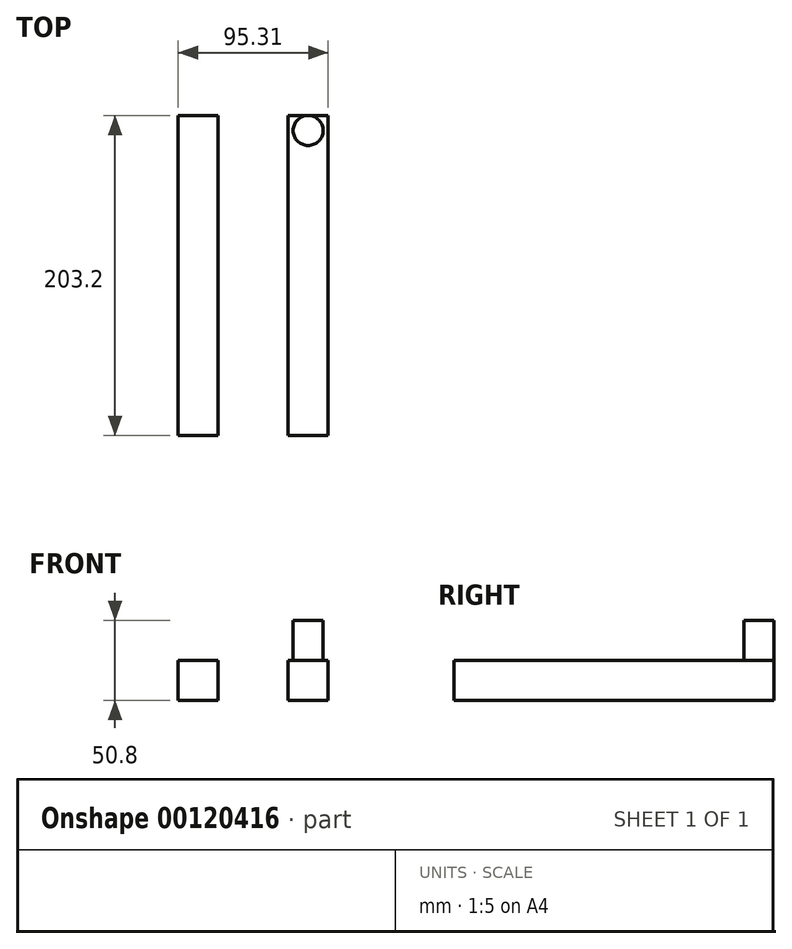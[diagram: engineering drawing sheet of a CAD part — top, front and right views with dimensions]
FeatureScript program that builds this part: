
annotation { "Feature Type Name" : "Feature", "Feature Type Description" : "" }
export const myFeature = defineFeature(function(context is Context, id is Id, definition is map)
    precondition{}
    {
        {
            var Q0;
            Q0=qCreatedBy(makeId("Front.planeOp"),FACE);
            var sketch = newSketch(context, id + "F0", { "sketchPlane" : qUnion([Q0])});
            skLineSegment(sketch, "E0.bottom", {"start": v(0, 0) * mm, "end": v(25.4, 0) * mm});
            skLineSegment(sketch, "E0.top", {"start": v(0, 25.4) * mm, "end": v(25.4, 25.4) * mm});
            skLineSegment(sketch, "E0.left", {"start": v(0, 0) * mm, "end": v(0, 25.4) * mm});
            skLineSegment(sketch, "E0.right", {"start": v(25.4, 0) * mm, "end": v(25.4, 25.4) * mm});
            skSolve(sketch);
        }
        {
            var Q0;
            Q0 = qSketchRegion(id + "F0", true);
            extrude(context, id + "F1", {"entities" : qUnion([Q0]), "depth" : 203.2 * mm});
        }
        {
            var Q0;
            Q0=qCreatedBy(makeId("Front.planeOp"),FACE);
            var sketch = newSketch(context, id + "F2", { "sketchPlane" : qUnion([Q0])});
            skLineSegment(sketch, "E1.bottom", {"start": v(-69.91, 0) * mm, "end": v(-44.51, 0) * mm});
            skLineSegment(sketch, "E1.top", {"start": v(-69.91, 25.4) * mm, "end": v(-44.51, 25.4) * mm});
            skLineSegment(sketch, "E1.left", {"start": v(-69.91, 0) * mm, "end": v(-69.91, 25.4) * mm});
            skLineSegment(sketch, "E1.right", {"start": v(-44.51, 0) * mm, "end": v(-44.51, 25.4) * mm});
            skSolve(sketch);
        }
        {
            var Q0;
            Q0=makeQuery(id+"F2.imprint","IMPRINT",FACE,{"disambiguationData":[TD([[makeQuery(id+"F2.imprint","IMPRINT",EDGE,{"derivedFrom":sQuery(id+"F2.wireOp",EDGE,"E1.bottom")}),1.0]])]});
            extrude(context, id + "F3", {"entities" : qUnion([Q0]), "depth" : 203.2 * mm});
        }
        {
            var Q0;
            Q0=makeQuery(id+"F1.opExtrude","SWEPT_FACE",FACE,{"disambiguationData":[OSD([sQuery(id+"F0.wireOp",EDGE,"E0.top")])]});
            var sketch = newSketch(context, id + "F4", { "sketchPlane" : qUnion([Q0])});
            skPoint(sketch, "E2.endSnap0", {"position": v(12.7, 0) * mm});
            skCircle(sketch, "E3", {"center": v(12.7, -9.53) * mm, "radius": 9.53 * mm});
            skSolve(sketch);
        }
        {
            var Q0;
            Q0 = qSketchRegion(id + "F4", true);
            extrude(context, id + "F5", {"entities" : qUnion([Q0]), "operationType" : NewBodyOperationType.ADD, "depth" : 25.4 * mm});
        }
    });
